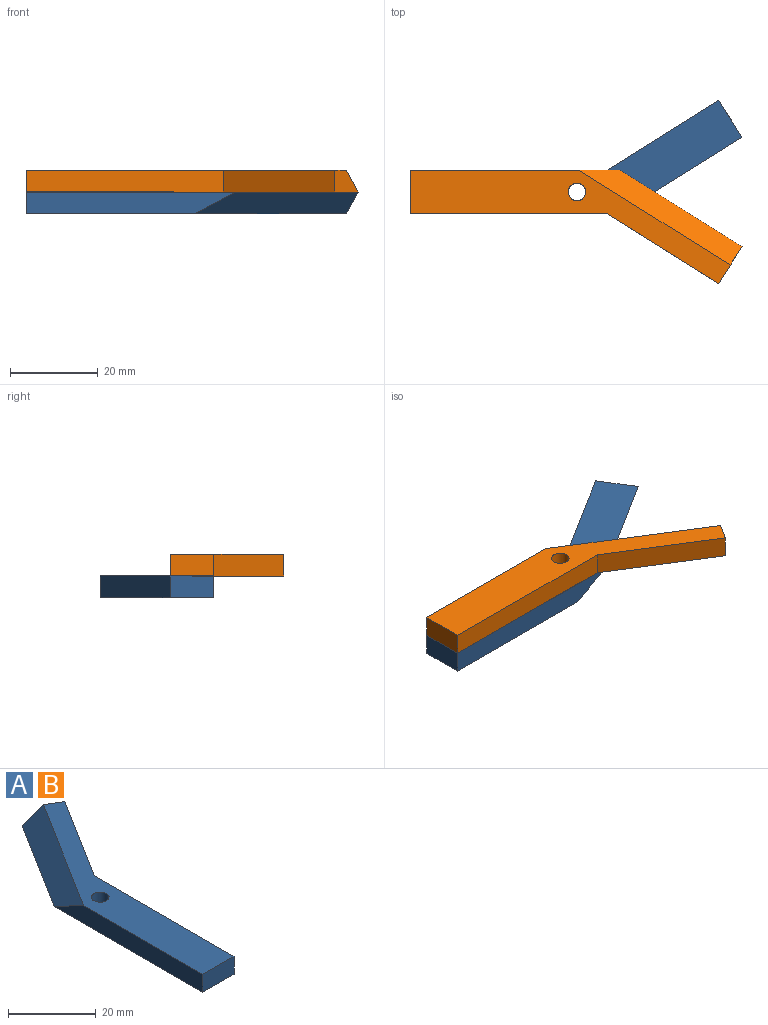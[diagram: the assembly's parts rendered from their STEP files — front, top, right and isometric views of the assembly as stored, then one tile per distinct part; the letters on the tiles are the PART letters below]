
ASSEMBLY  parts=2 mates=1
PART A: 9 faces, bbox 25.9x75.7x5 mm
  f0: plane 47.87x5mm, normal (-1,0,0), area 215.8mm2, adj f1,f6,f7,f8
  f1: plane 10x5mm, normal (0,-1,0), area 50mm2, adj f0,f2,f6,f7
  f2: plane 45x5mm, normal (1,0,0), area 225mm2, adj f1,f3,f6,f7
  f3: plane 25.43x15.92mm, normal (0.85,-0.53,0), area 150mm2, adj f2,f4,f6,f7
  f4: plane 8.48x5.31mm, normal (0.53,0.85,0), area 37.5mm2, adj f3,f6,f7,f8
  f5: cylinder r=2mm len=5mm, axis (0,0,-1), area 62.8mm2, adj f6,f7
  f6: plane 73.08x25.92mm, normal (0,0,1), area 581.8mm2, adj f0,f1,f2,f3,f4,f5,f8
  f7: plane 75.74x25.92mm, normal (0,0,-1), area 766.1mm2, adj f0,f1,f2,f3,f4,f5,f8
  f8: plane 37.29x21.68mm, normal (-0.6,0.38,0.71), area 260.7mm2, adj f0,f4,f6,f7
PART B: same geometry as A
PLACE A rot(axis=(-0.71,-0.71,0),180deg) t=(27.09,-14.07,15.53)mm
PLACE B rot(axis=(0,0,-1),90deg) t=(27.09,-14.07,15.53)mm
MATE revolute B.f5 <-> A.f5  axis (0,0,-1) through (24.07,-14.07,15.53)mm
